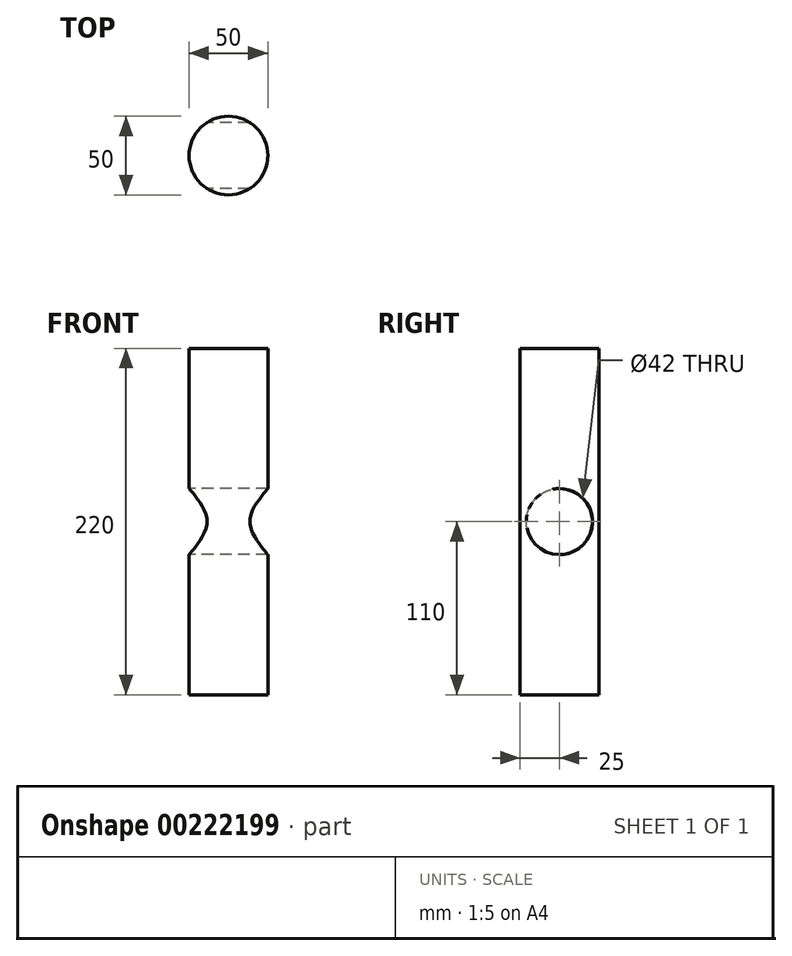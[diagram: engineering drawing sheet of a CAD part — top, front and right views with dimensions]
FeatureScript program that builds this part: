
annotation { "Feature Type Name" : "Feature", "Feature Type Description" : "" }
export const myFeature = defineFeature(function(context is Context, id is Id, definition is map)
    precondition{}
    {
        {
            var Q0;
            Q0=qCreatedBy(makeId("Top.planeOp"),FACE);
            var sketch = newSketch(context, id + "F0", { "sketchPlane" : qUnion([Q0])});
            skCircle(sketch, "E0", {"center": v(0, 0) * mm, "radius": 25 * mm});
            skSolve(sketch);
        }
        {
            var Q0;
            Q0=makeQuery(id+"F0.imprint","IMPRINT",FACE,{"disambiguationData":[TD([[makeQuery(id+"F0.imprint","IMPRINT",EDGE,{"derivedFrom":sQuery(id+"F0.wireOp",EDGE,"E0")}),1.0]])]});
            extrude(context, id + "F1", {"entities" : qUnion([Q0]), "depth" : 110 * mm, "hasSecondDirection" : true, "secondDirectionOppositeDirection" : true, "secondDirectionDepth" : 110 * mm});
        }
        {
            var Q0;
            Q0=qCreatedBy(makeId("Right.planeOp"),FACE);
            var sketch = newSketch(context, id + "F2", { "sketchPlane" : qUnion([Q0])});
            skCircle(sketch, "E1", {"center": v(0, 0) * mm, "radius": 21 * mm});
            skSolve(sketch);
        }
        {
            var Q0;
            Q0 = qSketchRegion(id + "F2", true);
            extrude(context, id + "F3", {"entities" : qUnion([Q0]), "operationType" : NewBodyOperationType.REMOVE, "depth" : 25 * mm, "hasSecondDirection" : true, "secondDirectionOppositeDirection" : true, "secondDirectionDepth" : 25 * mm});
        }
        {
            var Q0;
            Q0=sQuery(id+"F2.wireOp",EDGE,"E1");
            extrude(context, id + "F4", {"bodyType" : ToolBodyType.SURFACE, "surfaceEntities" : qUnion([Q0]), "depth" : 25 * mm, "hasSecondDirection" : true, "secondDirectionOppositeDirection" : true, "secondDirectionDepth" : 25 * mm});
        }
    });
